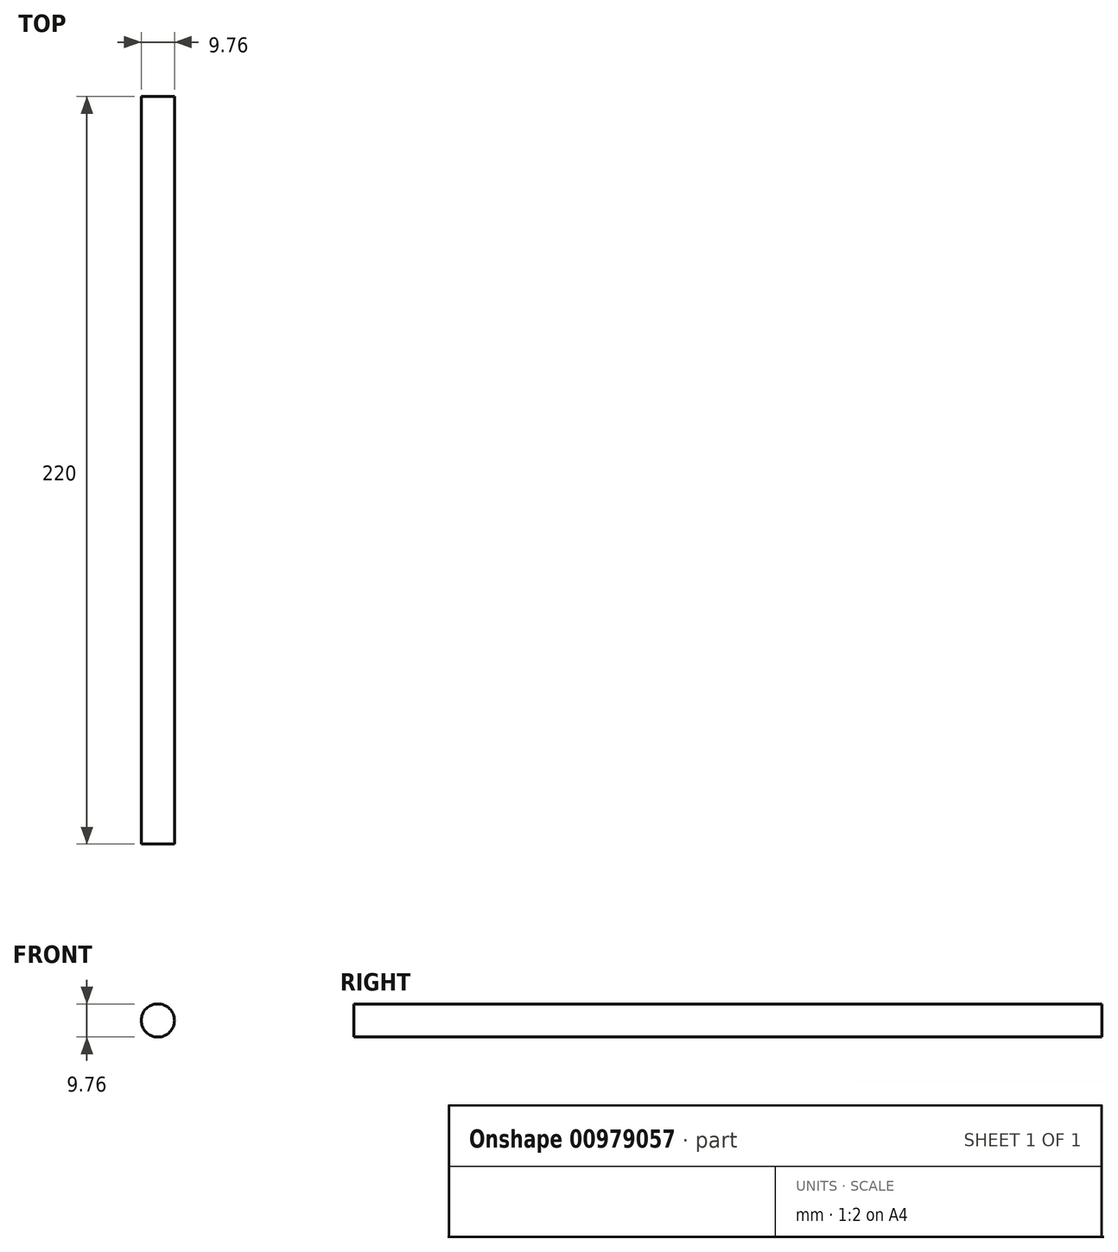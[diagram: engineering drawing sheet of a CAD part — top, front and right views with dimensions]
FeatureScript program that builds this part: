
annotation { "Feature Type Name" : "Feature", "Feature Type Description" : "" }
export const myFeature = defineFeature(function(context is Context, id is Id, definition is map)
    precondition{}
    {
        {
            var Q0;
            Q0=qCreatedBy(makeId("Front.planeOp"),FACE);
            var sketch = newSketch(context, id + "F0", { "sketchPlane" : qUnion([Q0])});
            skCircle(sketch, "E0", {"center": v(0, 0) * mm, "radius": 4.88 * mm});
            skSolve(sketch);
        }
        {
            var Q0;
            Q0=makeQuery(id+"F0.imprint","IMPRINT",FACE,{"disambiguationData":[TD([[makeQuery(id+"F0.imprint","IMPRINT",EDGE,{"derivedFrom":sQuery(id+"F0.wireOp",EDGE,"E0")}),1.0]])]});
            extrude(context, id + "F1", {"entities" : qUnion([Q0]), "depth" : 220 * mm, "offsetDistance" : 25 * mm});
        }
    });
